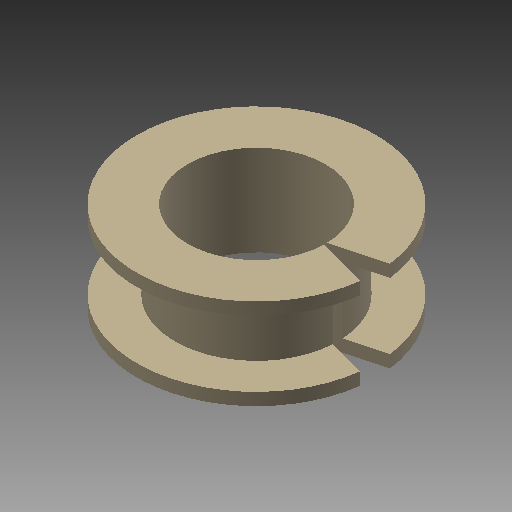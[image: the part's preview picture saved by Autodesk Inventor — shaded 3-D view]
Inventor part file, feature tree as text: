
AUTODESK INVENTOR PART (.ipt)
format: ipt  version: 2019 (Build 230136000, 136)  size: 134,656 bytes
history: native  units: mm
features: sketch x2, revolve x1, extrude x1
ambient origin geometry x8: Origin, YZ Plane, XZ Plane, XY Plane, X Axis, Y Axis, Z Axis, Center Point
bodies: Solid1 (feature_tree)
feature tree (4):
  revolve  "Revolution1"  [1 undecoded]
  extrude  "Extrusion2"  Depth=0.75mm
  sketch  "Sketch1"  dims[d0=8.36mm d1=9.89mm]
  sketch  "Sketch3"  dims[d2=14.5mm d3=0.75mm d4=4.0mm d5=0.75mm d6=90.0deg d15=15.0deg d16=30.0deg d17=3.01401mm d18=3.01401mm d19=10.0mm d20=0.0mm]
note: 1 required parameter value undecoded (feature->parameter linkage not recoverable at this tier; creation-order binding heuristic only, values carry confidence <= 0.55)
